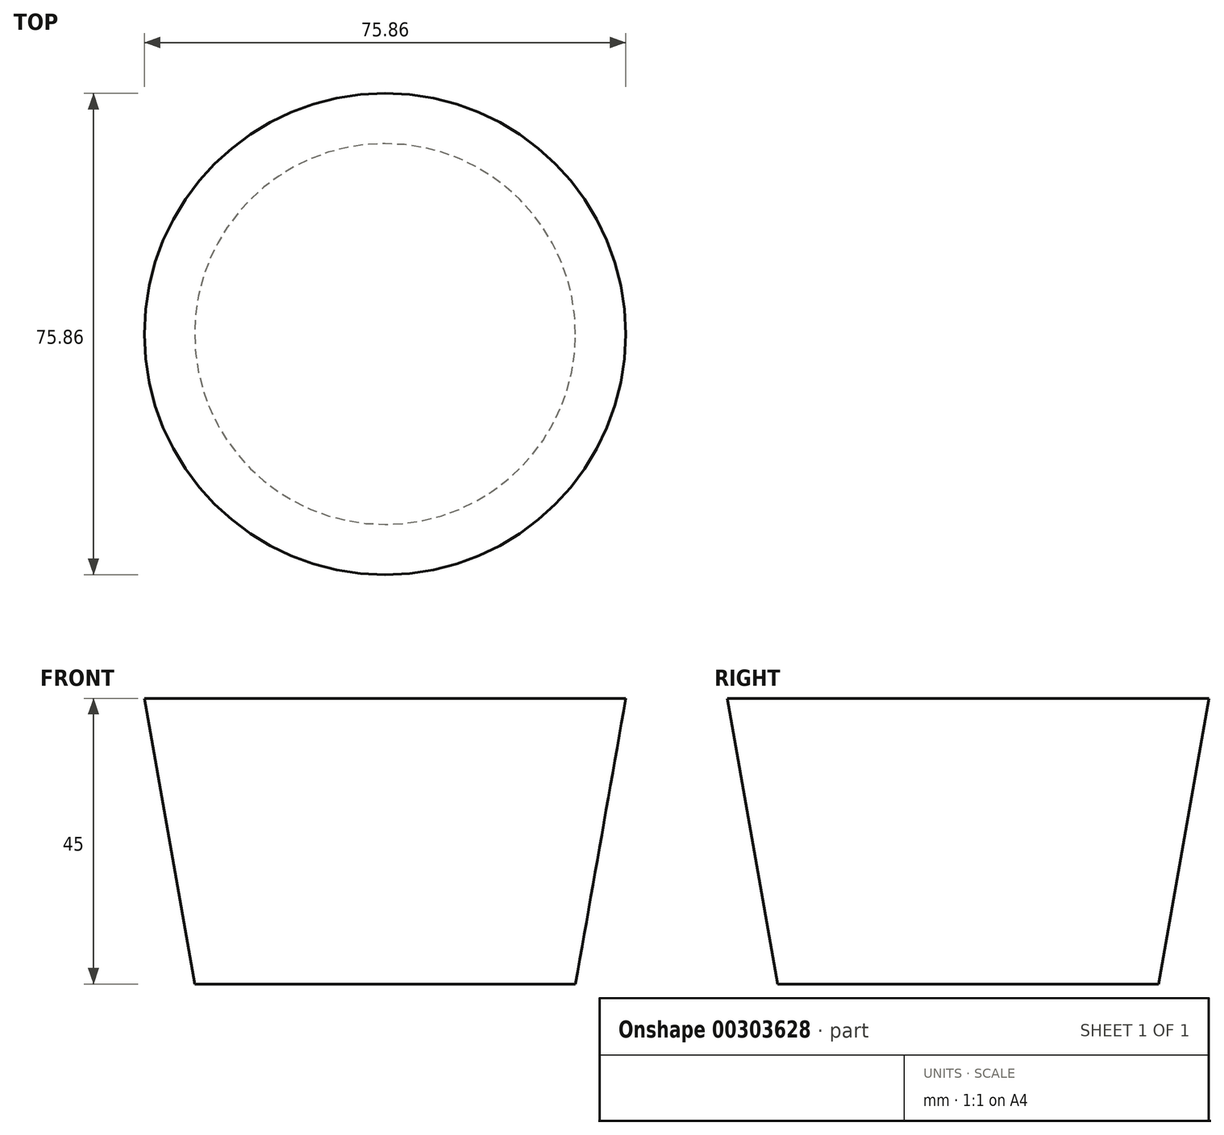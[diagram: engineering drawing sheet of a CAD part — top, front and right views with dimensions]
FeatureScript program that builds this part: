
annotation { "Feature Type Name" : "Feature", "Feature Type Description" : "" }
export const myFeature = defineFeature(function(context is Context, id is Id, definition is map)
    precondition{}
    {
        {
            var Q0;
            Q0=qCreatedBy(makeId("Top.planeOp"),FACE);
            var sketch = newSketch(context, id + "F0", { "sketchPlane" : qUnion([Q0])});
            skCircle(sketch, "E0", {"center": v(0, 0) * mm, "radius": 30 * mm});
            skSolve(sketch);
        }
        {
            var Q0;
            Q0 = qSketchRegion(id + "F0", true);
            extrude(context, id + "F1", {"entities" : qUnion([Q0]), "depth" : 45 * mm, "hasDraft" : true, "draftAngle" : 10 * degree});
        }
    });
